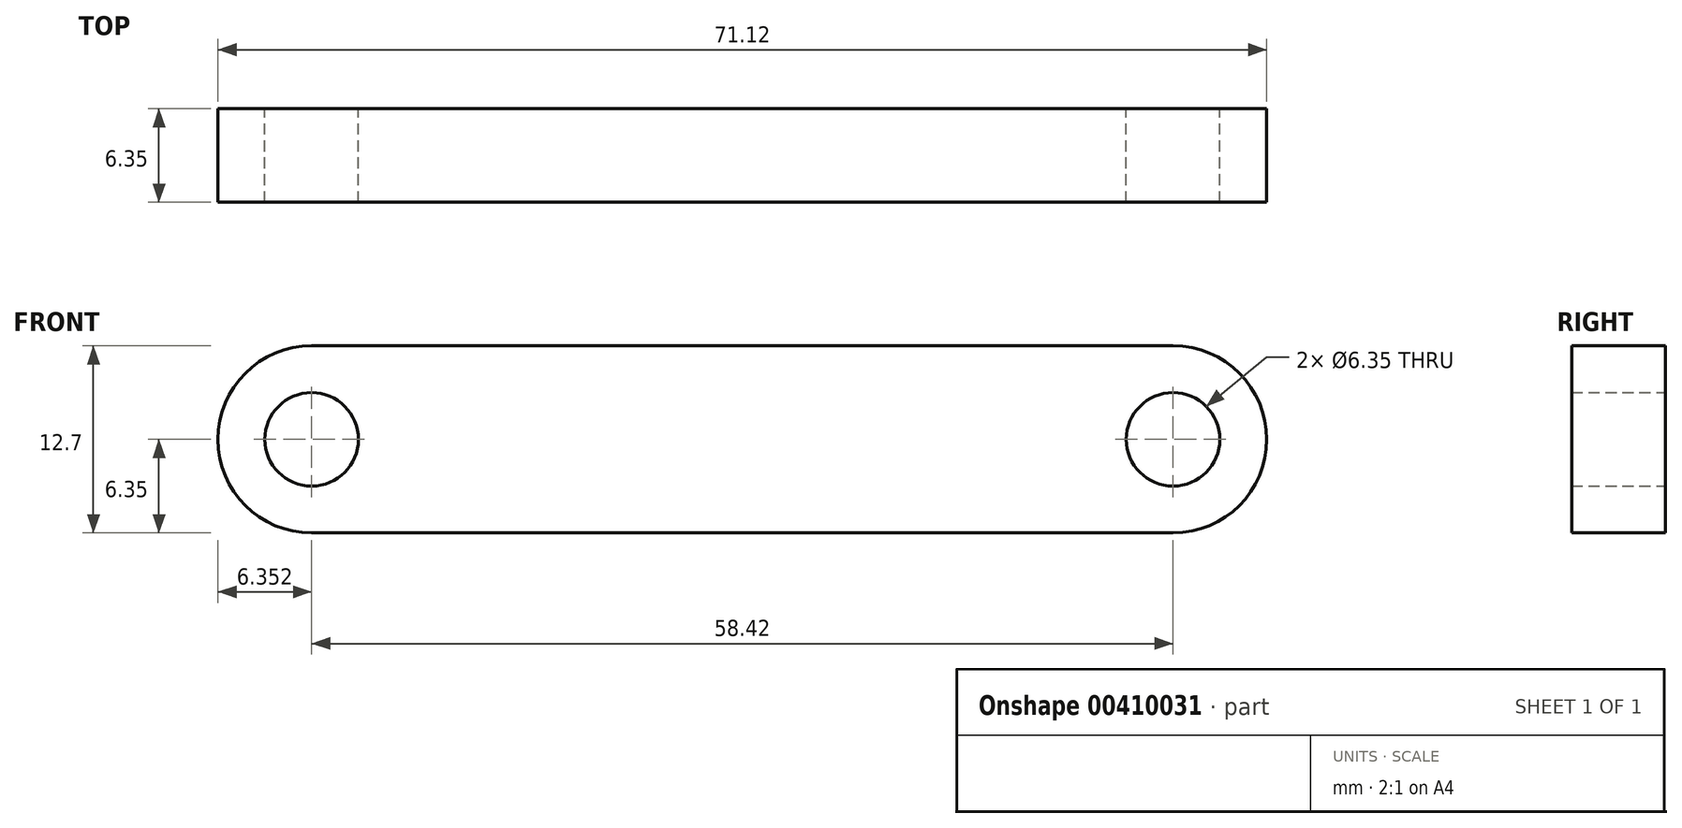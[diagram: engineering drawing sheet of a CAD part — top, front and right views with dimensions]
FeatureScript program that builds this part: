
annotation { "Feature Type Name" : "Feature", "Feature Type Description" : "" }
export const myFeature = defineFeature(function(context is Context, id is Id, definition is map)
    precondition{}
    {
        {
            var Q0;
            Q0=qCreatedBy(makeId("Front.planeOp"),FACE);
            var sketch = newSketch(context, id + "F0", { "sketchPlane" : qUnion([Q0])});
            skArc(sketch, "E0", {"start": v(2.66, 6.35) * mm, "mid": v(-3.69, 0) * mm, "end": v(2.66, -6.35) * mm});
            skArc(sketch, "E1", {"start": v(61.08, -6.35) * mm, "mid": v(67.43, 0) * mm, "end": v(61.08, 6.35) * mm});
            skLineSegment(sketch, "E2", {"start": v(2.66, -6.35) * mm, "end": v(61.08, -6.35) * mm});
            skLineSegment(sketch, "E3", {"start": v(2.66, 6.35) * mm, "end": v(61.08, 6.35) * mm});
            skCircle(sketch, "E4", {"center": v(2.66, 0) * mm, "radius": 3.18 * mm});
            skCircle(sketch, "E5", {"center": v(61.08, 0) * mm, "radius": 3.18 * mm});
            skSolve(sketch);
        }
        {
            var Q0;
            Q0=makeQuery(id+"F0.imprint","IMPRINT",FACE,{"disambiguationData":[TD([[makeQuery(id+"F0.imprint","IMPRINT",EDGE,{"derivedFrom":sQuery(id+"F0.wireOp",EDGE,"E0")}),1.0]])]});
            extrude(context, id + "F1", {"entities" : qUnion([Q0]), "depth" : 6.35 * mm});
        }
    });
